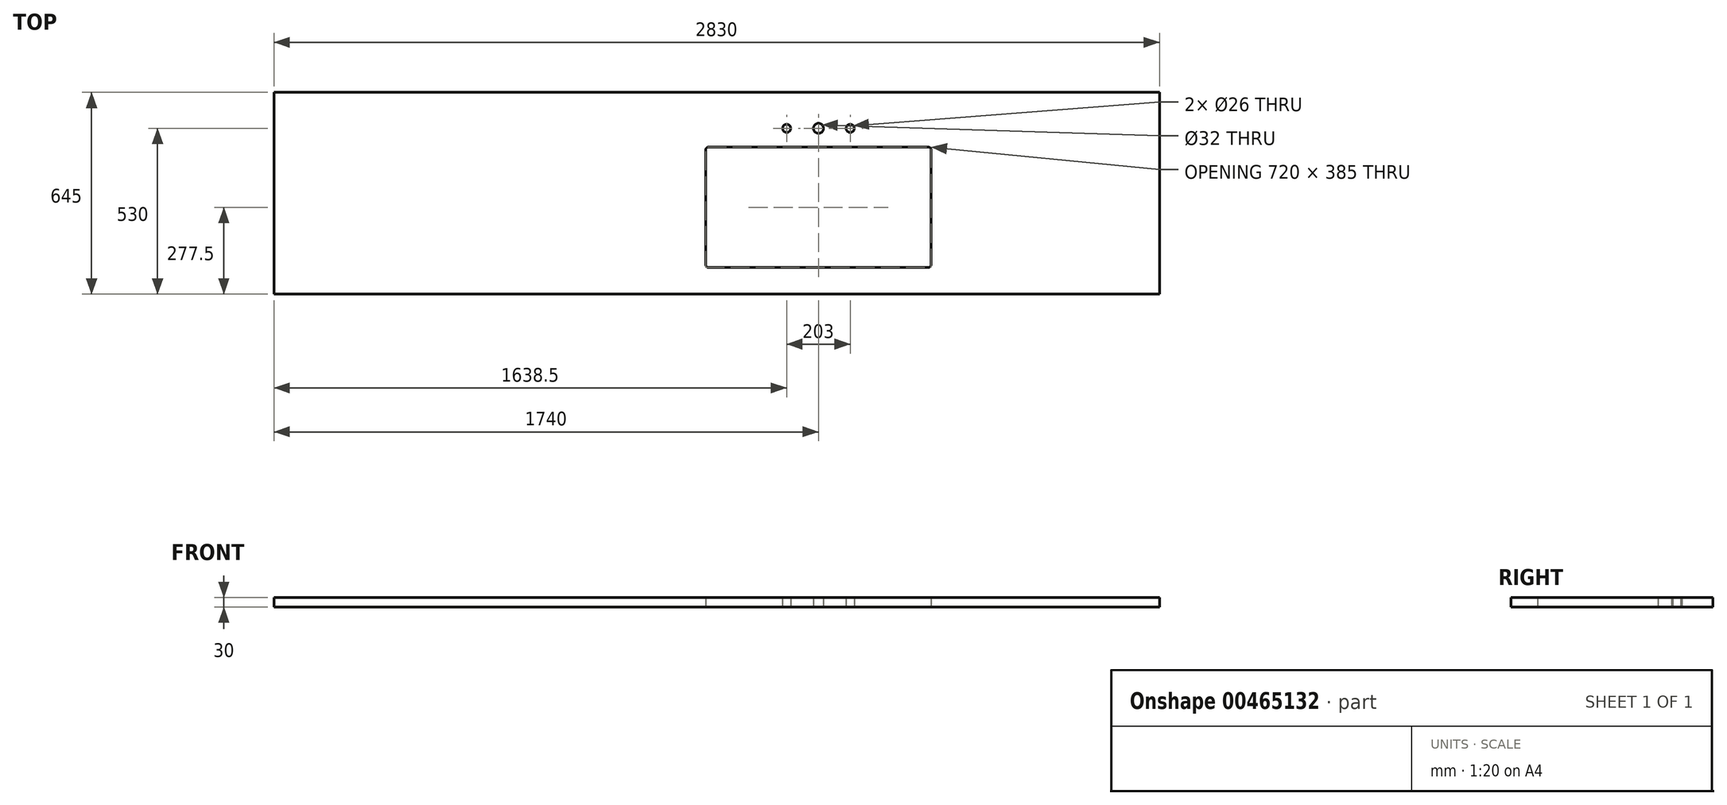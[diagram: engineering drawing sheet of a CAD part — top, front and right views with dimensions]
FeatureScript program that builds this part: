
annotation { "Feature Type Name" : "Feature", "Feature Type Description" : "" }
export const myFeature = defineFeature(function(context is Context, id is Id, definition is map)
    precondition{}
    {
        {
            var Q0;
            Q0=qCreatedBy(makeId("Top.planeOp"),FACE);
            var sketch = newSketch(context, id + "F0", { "sketchPlane" : qUnion([Q0])});
            skLineSegment(sketch, "E0.bottom", {"start": v(0, 0) * mm, "end": v(-2830, 0) * mm});
            skLineSegment(sketch, "E0.top", {"start": v(0, 645) * mm, "end": v(-2830, 645) * mm});
            skLineSegment(sketch, "E0.left", {"start": v(0, 0) * mm, "end": v(0, 645) * mm});
            skLineSegment(sketch, "E0.right", {"start": v(-2830, 0) * mm, "end": v(-2830, 645) * mm});
            skLineSegment(sketch, "E1.bottom", {"start": v(-1441, 470) * mm, "end": v(-739, 470) * mm});
            skLineSegment(sketch, "E1.top", {"start": v(-1441, 85) * mm, "end": v(-739, 85) * mm});
            skLineSegment(sketch, "E1.left", {"start": v(-1450, 461) * mm, "end": v(-1450, 94) * mm});
            skLineSegment(sketch, "E1.right", {"start": v(-730, 461) * mm, "end": v(-730, 94) * mm});
            skPoint(sketch, "E2.visualSharp", {"position": v(-1450, 470) * mm});
            skArc(sketch, "E2.filletArc", {"start": v(-1441, 470) * mm, "mid": v(-1447.36, 467.36) * mm, "end": v(-1450, 461) * mm});
            skPoint(sketch, "E3.visualSharp", {"position": v(-730, 470) * mm});
            skArc(sketch, "E3.filletArc", {"start": v(-730, 461) * mm, "mid": v(-732.64, 467.36) * mm, "end": v(-739, 470) * mm});
            skPoint(sketch, "E4.visualSharp", {"position": v(-1450, 85) * mm});
            skArc(sketch, "E4.filletArc", {"start": v(-1450, 94) * mm, "mid": v(-1447.36, 87.64) * mm, "end": v(-1441, 85) * mm});
            skPoint(sketch, "E5.visualSharp", {"position": v(-730, 85) * mm});
            skArc(sketch, "E5.filletArc", {"start": v(-739, 85) * mm, "mid": v(-732.64, 87.64) * mm, "end": v(-730, 94) * mm});
            skLineSegment(sketch, "E6", {"start": v(-1090, 470) * mm, "end": v(-1090, 85) * mm, "construction": true});
            skLineSegment(sketch, "E7", {"start": v(-1090, 470) * mm, "end": v(-1090, 734.67) * mm, "construction": true});
            skCircle(sketch, "E8", {"center": v(-1090, 530) * mm, "radius": 16 * mm});
            skCircle(sketch, "E9", {"center": v(-1191.5, 530) * mm, "radius": 13 * mm});
            skCircle(sketch, "E10", {"center": v(-988.5, 530) * mm, "radius": 13 * mm});
            skLineSegment(sketch, "E11", {"start": v(-1407.53, 530) * mm, "end": v(-786.15, 530) * mm, "construction": true});
            skSolve(sketch);
        }
        {
            var Q0;
            Q0 = qSketchRegion(id + "F0", true);
            extrude(context, id + "F1", {"entities" : qUnion([Q0]), "depth" : 30 * mm});
        }
    });
